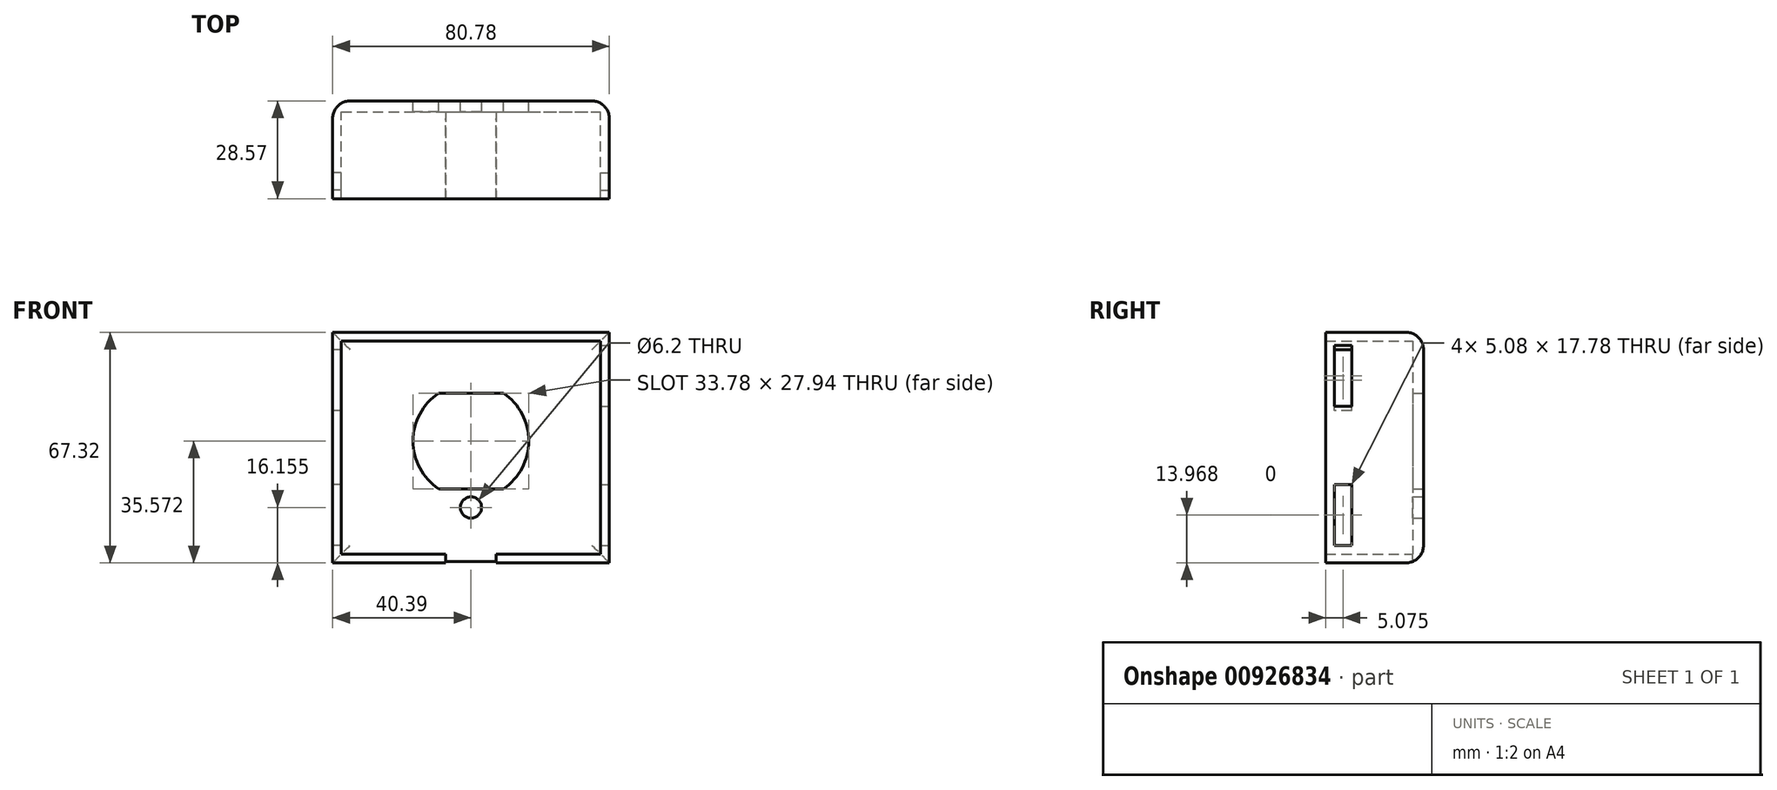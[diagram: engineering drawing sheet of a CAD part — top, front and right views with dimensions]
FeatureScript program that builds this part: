
annotation { "Feature Type Name" : "Feature", "Feature Type Description" : "" }
export const myFeature = defineFeature(function(context is Context, id is Id, definition is map)
    precondition{}
    {
        {
            var Q0;
            Q0=qCreatedBy(makeId("Front.planeOp"),FACE);
            var sketch = newSketch(context, id + "F0", { "sketchPlane" : qUnion([Q0])});
            skLineSegment(sketch, "E0", {"start": v(-9.5, -12.06) * mm, "end": v(9.5, -12.06) * mm});
            skCircle(sketch, "E1", {"center": v(0, -17.5) * mm, "radius": 3.1 * mm});
            skLineSegment(sketch, "E2.bottom", {"start": v(40.39, 33.66) * mm, "end": v(-40.39, 33.66) * mm});
            skLineSegment(sketch, "E2.top", {"start": v(40.39, -33.66) * mm, "end": v(-40.39, -33.66) * mm});
            skLineSegment(sketch, "E2.left", {"start": v(40.39, 33.66) * mm, "end": v(40.39, -33.66) * mm});
            skLineSegment(sketch, "E2.right", {"start": v(-40.39, 33.66) * mm, "end": v(-40.39, -33.66) * mm});
            skPoint(sketch, "E2.middle", {"position": v(0, 0) * mm});
            skPoint(sketch, "E3", {"position": v(0, 9.53) * mm});
            skLineSegment(sketch, "E4", {"start": v(-9.5, 15.88) * mm, "end": v(9.5, 15.88) * mm});
            skArc(sketch, "E5", {"start": v(-9.5, 15.88) * mm, "mid": v(-16.9, 1.91) * mm, "end": v(-9.5, -12.06) * mm});
            skArc(sketch, "E6", {"start": v(9.5, -12.06) * mm, "mid": v(16.9, 1.91) * mm, "end": v(9.5, 15.88) * mm});
            skSolve(sketch);
        }
        {
            var Q0;
            Q0=makeQuery(id+"F0.imprint","IMPRINT",FACE,{"disambiguationData":[TD([[makeQuery(id+"F0.imprint","IMPRINT",EDGE,{"derivedFrom":sQuery(id+"F0.wireOp",EDGE,"E0")}),-1.0]])]});
            extrude(context, id + "F1", {"entities" : qUnion([Q0]), "depth" : 3.17 * mm, "offsetDistance" : 25.4 * mm});
        }
        {
            var Q0;
            Q0=makeQuery(id+"F1.opExtrude","CAP_FACE",FACE,{"disambiguationData":[OSD([sQuery(id+"F0.wireOp",EDGE,"E0"),sQuery(id+"F0.wireOp",EDGE,"E1"),sQuery(id+"F0.wireOp",EDGE,"E2.bottom"),sQuery(id+"F0.wireOp",EDGE,"E2.top"),sQuery(id+"F0.wireOp",EDGE,"E2.left"),sQuery(id+"F0.wireOp",EDGE,"E2.right"),sQuery(id+"F0.wireOp",EDGE,"E4"),sQuery(id+"F0.wireOp",EDGE,"E5"),sQuery(id+"F0.wireOp",EDGE,"E6")])],"isStart":false});
            var sketch = newSketch(context, id + "F2", { "sketchPlane" : qUnion([Q0])});
            skLineSegment(sketch, "E7.bottom", {"start": v(-37.85, 31.12) * mm, "end": v(37.85, 31.12) * mm});
            skLineSegment(sketch, "E7.top", {"start": v(-37.85, -31.12) * mm, "end": v(37.85, -31.12) * mm});
            skLineSegment(sketch, "E7.left", {"start": v(-37.85, 31.12) * mm, "end": v(-37.85, -31.12) * mm});
            skLineSegment(sketch, "E7.right", {"start": v(37.85, 31.12) * mm, "end": v(37.85, -31.12) * mm});
            skSolve(sketch);
        }
        {
            var Q0;
            Q0=makeQuery(id+"F2.imprint","IMPRINT",FACE,{"disambiguationData":[TD([[makeQuery(id+"F2.imprint","IMPRINT",EDGE,{"derivedFrom":sQuery(id+"F2.wireOp",EDGE,"E7.bottom")}),1.0]])]});
            extrude(context, id + "F3", {"entities" : qUnion([Q0]), "operationType" : NewBodyOperationType.ADD, "depth" : 25.4 * mm, "offsetDistance" : 25.4 * mm});
        }
        {
            var Q0;
            Q0=makeQuery(id+"F3.opExtrude","SWEPT_FACE",FACE,{"disambiguationData":[OSD([sQuery(id+"F2.wireOp",EDGE,"E7.top")])]});
            var sketch = newSketch(context, id + "F4", { "sketchPlane" : qUnion([Q0])});
            skLineSegment(sketch, "E8.bottom", {"start": v(-7.37, -3.18) * mm, "end": v(7.37, -3.18) * mm});
            skLineSegment(sketch, "E8.top", {"start": v(-7.37, -28.58) * mm, "end": v(7.37, -28.58) * mm});
            skLineSegment(sketch, "E8.left", {"start": v(-7.37, -3.18) * mm, "end": v(-7.37, -28.58) * mm});
            skLineSegment(sketch, "E8.right", {"start": v(7.37, -3.17) * mm, "end": v(7.37, -28.58) * mm});
            skSolve(sketch);
        }
        {
            var Q0;
            Q0 = qSketchRegion(id + "F4", true);
            extrude(context, id + "F5", {"entities" : qUnion([Q0]), "operationType" : NewBodyOperationType.REMOVE, "oppositeDirection" : true, "depth" : 25.4 * mm, "offsetDistance" : 25.4 * mm});
        }
        {
            var Q0;
            {var subQ0=sQuery(id+"F0.wireOp",EDGE,"E2.left");Q0=makeQuery(id+"F3.boolean.opBoolean","MERGE",FACE,{"derivedFrom":[makeQuery(id+"F1.opExtrude","SWEPT_FACE",FACE,{"disambiguationData":[OSD([subQ0])]}),makeQuery(id+"F3.opExtrude","SWEPT_FACE",FACE,{"disambiguationData":[OSD([subQ0])]})]});}
            var sketch = newSketch(context, id + "F6", { "sketchPlane" : qUnion([Q0])});
            skLineSegment(sketch, "E9.bottom", {"start": v(-26.04, 29.85) * mm, "end": v(-20.96, 29.85) * mm});
            skLineSegment(sketch, "E9.top", {"start": v(-26.04, 12.07) * mm, "end": v(-20.96, 12.07) * mm});
            skLineSegment(sketch, "E9.left", {"start": v(-26.04, 29.85) * mm, "end": v(-26.04, 12.07) * mm});
            skLineSegment(sketch, "E9.right", {"start": v(-20.96, 29.85) * mm, "end": v(-20.96, 12.07) * mm});
            skLineSegment(sketch, "E10.bottom", {"start": v(-26.04, -10.8) * mm, "end": v(-20.96, -10.8) * mm});
            skLineSegment(sketch, "E10.top", {"start": v(-26.04, -28.58) * mm, "end": v(-20.96, -28.58) * mm});
            skLineSegment(sketch, "E10.left", {"start": v(-26.04, -10.8) * mm, "end": v(-26.04, -28.58) * mm});
            skLineSegment(sketch, "E10.right", {"start": v(-20.96, -10.8) * mm, "end": v(-20.96, -28.58) * mm});
            skSolve(sketch);
        }
        {
            var Q0;
            Q0=makeQuery(id+"F6.imprint","IMPRINT",FACE,{"disambiguationData":[TD([[makeQuery(id+"F6.imprint","IMPRINT",EDGE,{"derivedFrom":sQuery(id+"F6.wireOp",EDGE,"E9.bottom")}),-1.0]])]});
            var Q1;
            Q1=makeQuery(id+"F6.imprint","IMPRINT",FACE,{"disambiguationData":[TD([[makeQuery(id+"F6.imprint","IMPRINT",EDGE,{"derivedFrom":sQuery(id+"F6.wireOp",EDGE,"E10.bottom")}),-1.0]])]});
            extrude(context, id + "F7", {"entities" : qUnion([Q0, Q1]), "operationType" : NewBodyOperationType.REMOVE, "oppositeDirection" : true, "depth" : 25.4 * mm, "offsetDistance" : 25.4 * mm});
        }
        {
            var Q0;
            {var subQ0=sQuery(id+"F0.wireOp",EDGE,"E2.right");Q0=makeQuery(id+"F3.boolean.opBoolean","MERGE",FACE,{"derivedFrom":[makeQuery(id+"F1.opExtrude","SWEPT_FACE",FACE,{"disambiguationData":[OSD([subQ0])]}),makeQuery(id+"F3.opExtrude","SWEPT_FACE",FACE,{"disambiguationData":[OSD([subQ0])]})]});}
            var sketch = newSketch(context, id + "F8", { "sketchPlane" : qUnion([Q0])});
            skLineSegment(sketch, "E11.bottom", {"start": v(20.95, 28.58) * mm, "end": v(26.04, 28.58) * mm});
            skLineSegment(sketch, "E11.top", {"start": v(20.95, 10.8) * mm, "end": v(26.04, 10.8) * mm});
            skLineSegment(sketch, "E11.left", {"start": v(20.95, 28.58) * mm, "end": v(20.95, 10.8) * mm});
            skLineSegment(sketch, "E11.right", {"start": v(26.04, 28.58) * mm, "end": v(26.04, 10.8) * mm});
            skLineSegment(sketch, "E12.bottom", {"start": v(20.96, -10.8) * mm, "end": v(26.04, -10.8) * mm});
            skLineSegment(sketch, "E12.top", {"start": v(20.96, -28.58) * mm, "end": v(26.04, -28.58) * mm});
            skLineSegment(sketch, "E12.left", {"start": v(20.96, -10.8) * mm, "end": v(20.96, -28.58) * mm});
            skLineSegment(sketch, "E12.right", {"start": v(26.04, -10.8) * mm, "end": v(26.04, -28.58) * mm});
            skSolve(sketch);
        }
        {
            var Q0;
            Q0=makeQuery(id+"F8.imprint","IMPRINT",FACE,{"disambiguationData":[TD([[makeQuery(id+"F8.imprint","IMPRINT",EDGE,{"derivedFrom":sQuery(id+"F8.wireOp",EDGE,"E11.bottom")}),-1.0]])]});
            var Q1;
            Q1=makeQuery(id+"F8.imprint","IMPRINT",FACE,{"disambiguationData":[TD([[makeQuery(id+"F8.imprint","IMPRINT",EDGE,{"derivedFrom":sQuery(id+"F8.wireOp",EDGE,"E12.bottom")}),-1.0]])]});
            extrude(context, id + "F9", {"entities" : qUnion([Q0, Q1]), "operationType" : NewBodyOperationType.REMOVE, "oppositeDirection" : true, "depth" : 25.4 * mm, "offsetDistance" : 25.4 * mm});
        }
        {
            var Q0;
            Q0=makeQuery(id+"F1.opExtrude","CAP_EDGE",EDGE,{"disambiguationData":[OSD([sQuery(id+"F0.wireOp",EDGE,"E2.bottom")])],"isStart":true});
            var Q1;
            Q1=makeQuery(id+"F1.opExtrude","CAP_EDGE",EDGE,{"disambiguationData":[OSD([sQuery(id+"F0.wireOp",EDGE,"E2.right")])],"isStart":true});
            var Q2;
            Q2=makeQuery(id+"F1.opExtrude","CAP_EDGE",EDGE,{"disambiguationData":[OSD([sQuery(id+"F0.wireOp",EDGE,"E2.left")])],"isStart":true});
            var Q3;
            Q3=makeQuery(id+"F1.opExtrude","CAP_EDGE",EDGE,{"disambiguationData":[OSD([sQuery(id+"F0.wireOp",EDGE,"E2.top")])],"isStart":true});
            fillet(context, id + "F10", {"entities" : qUnion([Q0, Q1, Q2, Q3]), "radius" : 5.08 * mm, "tangentPropagation" : true, "allowEdgeOverflow" : false});
        }
    });
